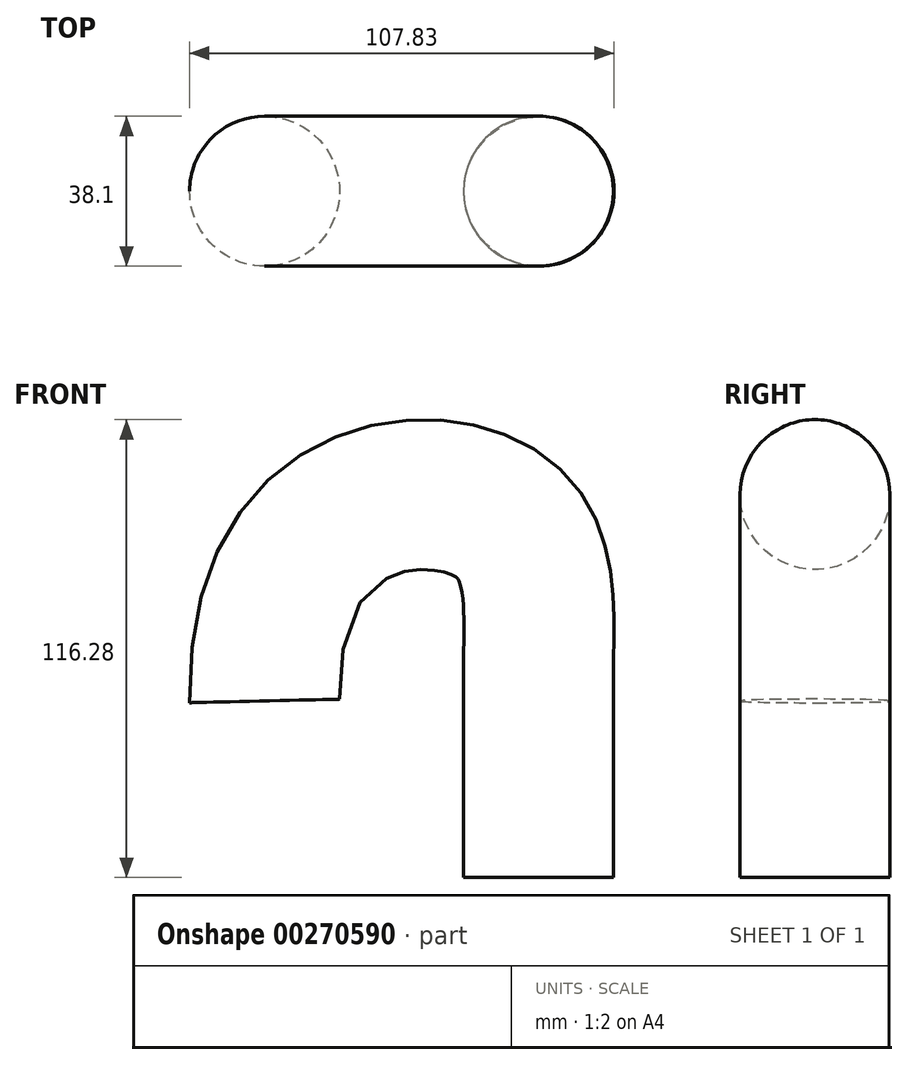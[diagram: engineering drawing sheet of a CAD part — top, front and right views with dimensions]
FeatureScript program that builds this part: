
annotation { "Feature Type Name" : "Feature", "Feature Type Description" : "" }
export const myFeature = defineFeature(function(context is Context, id is Id, definition is map)
    precondition{}
    {
        {
            var Q0;
            Q0=qCreatedBy(makeId("Top.planeOp"),FACE);
            var sketch = newSketch(context, id + "F0", { "sketchPlane" : qUnion([Q0])});
            skCircle(sketch, "E0", {"center": v(0, 0) * mm, "radius": 19.05 * mm});
            skSolve(sketch);
        }
        {
            var Q0;
            Q0=qCreatedBy(makeId("Front.planeOp"),FACE);
            var sketch = newSketch(context, id + "F1", { "sketchPlane" : qUnion([Q0])});
            skLineSegment(sketch, "E1", {"start": v(0, 0) * mm, "end": v(0, 50.8) * mm});
            skFitSpline(sketch, "E2", {"points": [v(0, 50.8) * mm, v(-10.63, 92.31) * mm, v(-69.57, 44.81) * mm], "startDerivative": vector(0, 115.68) * mm, "endDerivative": vector(6.78, -286.5) * mm});
            skSolve(sketch);
        }
        {
            var Q0;
            Q0=makeQuery(id+"F0.imprint","IMPRINT",FACE,{"disambiguationData":[TD([[makeQuery(id+"F0.imprint","IMPRINT",EDGE,{"derivedFrom":sQuery(id+"F0.wireOp",EDGE,"E0")}),1.0]])]});
            var Q1;
            Q1=sQuery(id+"F1.wireOp",EDGE,"E1");
            var Q2;
            Q2=sQuery(id+"F1.wireOp",EDGE,"E2");
            sweep(context, id + "F2", {"profiles" : qUnion([Q0]), "path" : qUnion([Q1, Q2])});
        }
    });
